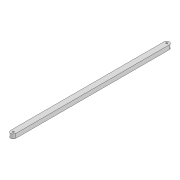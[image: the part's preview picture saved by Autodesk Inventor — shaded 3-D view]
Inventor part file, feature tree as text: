
AUTODESK INVENTOR PART (.ipt)
format: ipt  version: 2022 (Build 260153000, 153)  size: 82,432 bytes
history: native  units: mm
features: extrude x1, sketch x1
ambient origin geometry x8: Origin, YZ Plane, XZ Plane, XY Plane, X Axis, Y Axis, Z Axis, Center Point
bodies: Solid1 (feature_tree)
feature tree (2):
  extrude  "Extrusion1"  Depth=10.0mm
  sketch  "Sketch1"  dims[d0=289.365mm d1=10.0mm d2=3.0mm d3=3.0mm d4=8.0mm d5=0.0mm]
